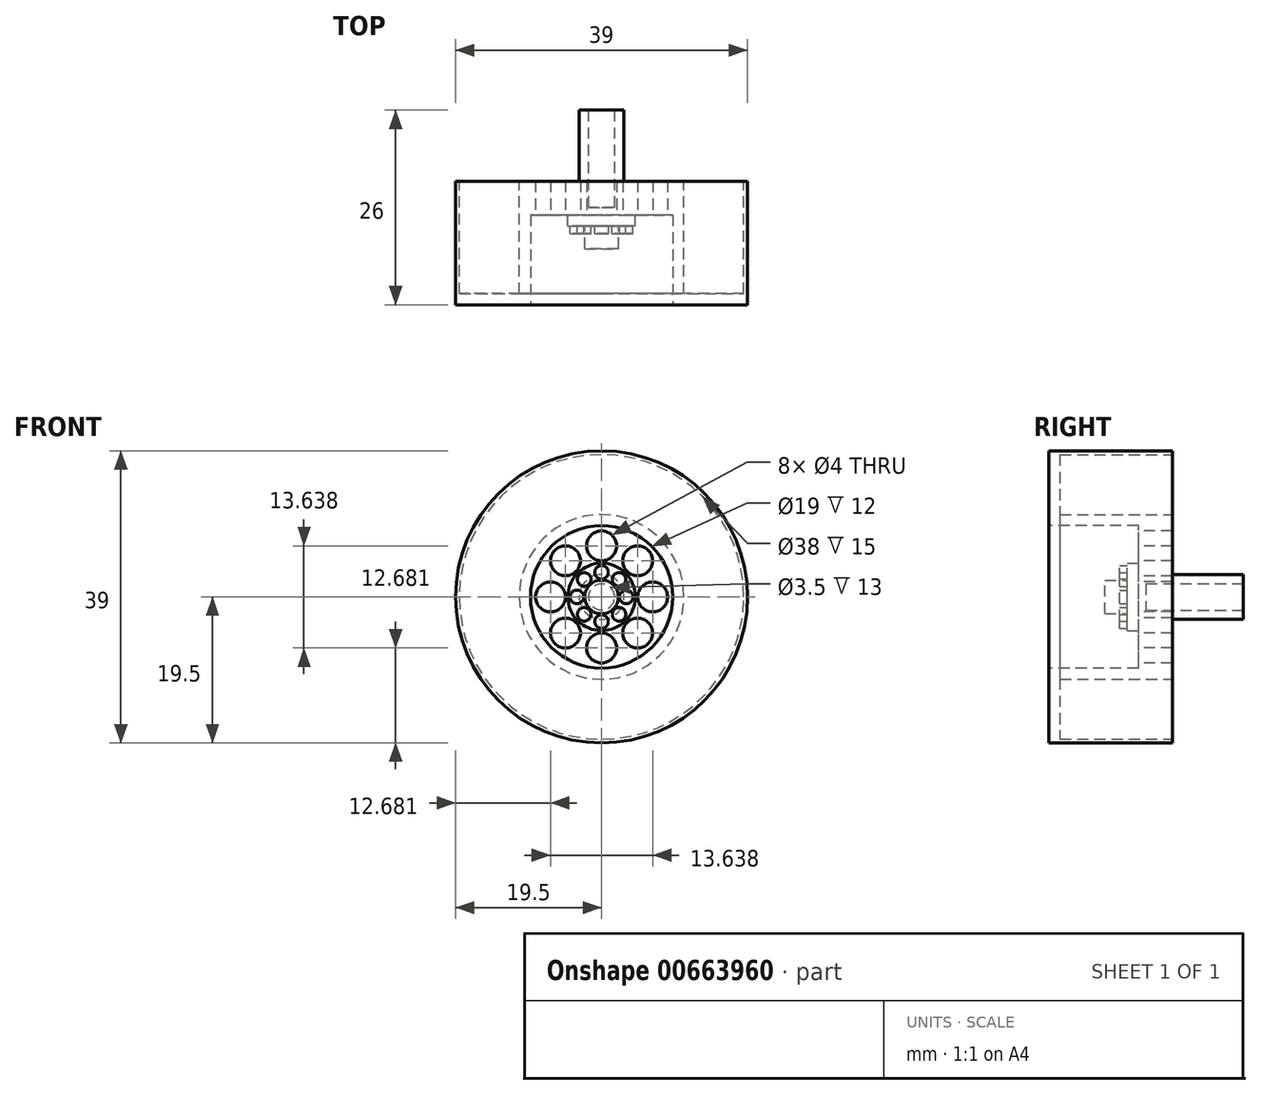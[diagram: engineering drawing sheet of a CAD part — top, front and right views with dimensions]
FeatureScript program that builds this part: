
annotation { "Feature Type Name" : "Feature", "Feature Type Description" : "" }
export const myFeature = defineFeature(function(context is Context, id is Id, definition is map)
    precondition{}
    {
        {
            var Q0;
            Q0=qCreatedBy(makeId("Front.planeOp"),FACE);
            var sketch = newSketch(context, id + "F0", { "sketchPlane" : qUnion([Q0])});
            skCircle(sketch, "E0", {"center": v(0, 0) * mm, "radius": 19.5 * mm});
            skSolve(sketch);
        }
        {
            var Q0;
            Q0=makeQuery(id+"F0.imprint","IMPRINT",FACE,{"disambiguationData":[TD([[makeQuery(id+"F0.imprint","IMPRINT",EDGE,{"derivedFrom":sQuery(id+"F0.wireOp",EDGE,"E0")}),1.0]])]});
            extrude(context, id + "F1", {"entities" : qUnion([Q0]), "oppositeDirection" : true, "depth" : 16.5 * mm, "offsetDistance" : 25 * mm});
        }
        {
            var Q0;
            Q0=qCreatedBy(makeId("Front.planeOp"),FACE);
            var sketch = newSketch(context, id + "F2", { "sketchPlane" : qUnion([Q0])});
            skCircle(sketch, "E1", {"center": v(0, 0) * mm, "radius": 9.5 * mm});
            skSolve(sketch);
        }
        {
            var Q0;
            Q0=makeQuery(id+"F2.imprint","IMPRINT",FACE,{"disambiguationData":[TD([[makeQuery(id+"F2.imprint","IMPRINT",EDGE,{"derivedFrom":sQuery(id+"F2.wireOp",EDGE,"E1")}),1.0]])]});
            var sketch = newSketch(context, id + "F3", { "sketchPlane" : qUnion([Q0])});
            skSolve(sketch);
        }
        {
            var Q0;
            Q0=makeQuery(id+"F3.imprint","IMPRINT",FACE,{"disambiguationData":[TD([[makeQuery(id+"F3.imprint","IMPRINT",EDGE,{"derivedFrom":makeQuery(id+"F2.imprint","IMPRINT",EDGE,{"derivedFrom":sQuery(id+"F2.wireOp",EDGE,"E1")})}),1.0]])]});
            extrude(context, id + "F4", {"entities" : qUnion([Q0]), "operationType" : NewBodyOperationType.REMOVE, "oppositeDirection" : true, "depth" : 12 * mm, "offsetDistance" : 25 * mm});
        }
        {
            var Q0;
            Q0=makeQuery(id+"F4.boolean.opBoolean","COPY",FACE,{"derivedFrom":makeQuery(id+"F4.opExtrude","CAP_FACE",FACE,{"disambiguationData":[OSD([sQuery(id+"F2.wireOp",EDGE,"E1")])],"isStart":false})});
            var sketch = newSketch(context, id + "F5", { "sketchPlane" : qUnion([Q0])});
            skCircle(sketch, "E2", {"center": v(0, 6.82) * mm, "radius": 2 * mm});
            skCircle(sketch, "E3.1.0", {"center": v(-4.82, 4.82) * mm, "radius": 2 * mm});
            skCircle(sketch, "E3.2.0", {"center": v(-6.82, 0) * mm, "radius": 2 * mm});
            skCircle(sketch, "E3.3.0", {"center": v(-4.82, -4.82) * mm, "radius": 2 * mm});
            skCircle(sketch, "E3.4.0", {"center": v(0, -6.82) * mm, "radius": 2 * mm});
            skCircle(sketch, "E3.5.0", {"center": v(4.82, -4.82) * mm, "radius": 2 * mm});
            skCircle(sketch, "E3.6.0", {"center": v(6.82, 0) * mm, "radius": 2 * mm});
            skCircle(sketch, "E3.7.0", {"center": v(4.82, 4.82) * mm, "radius": 2 * mm});
            skPoint(sketch, "E3.center", {"position": v(0, 0) * mm});
            skSolve(sketch);
        }
        {
            var Q0;
            Q0=makeQuery(id+"F5.imprint","IMPRINT",FACE,{"disambiguationData":[TD([[makeQuery(id+"F5.imprint","IMPRINT",EDGE,{"derivedFrom":sQuery(id+"F5.wireOp",EDGE,"E2")}),1.0]])]});
            var Q1;
            Q1=makeQuery(id+"F5.imprint","IMPRINT",FACE,{"disambiguationData":[TD([[makeQuery(id+"F5.imprint","IMPRINT",EDGE,{"derivedFrom":sQuery(id+"F5.wireOp",EDGE,"E3.7.0")}),1.0]])]});
            var Q2;
            Q2=makeQuery(id+"F5.imprint","IMPRINT",FACE,{"disambiguationData":[TD([[makeQuery(id+"F5.imprint","IMPRINT",EDGE,{"derivedFrom":sQuery(id+"F5.wireOp",EDGE,"E3.6.0")}),1.0]])]});
            var Q3;
            Q3=makeQuery(id+"F5.imprint","IMPRINT",FACE,{"disambiguationData":[TD([[makeQuery(id+"F5.imprint","IMPRINT",EDGE,{"derivedFrom":sQuery(id+"F5.wireOp",EDGE,"E3.5.0")}),1.0]])]});
            var Q4;
            Q4=makeQuery(id+"F5.imprint","IMPRINT",FACE,{"disambiguationData":[TD([[makeQuery(id+"F5.imprint","IMPRINT",EDGE,{"derivedFrom":sQuery(id+"F5.wireOp",EDGE,"E3.4.0")}),1.0]])]});
            var Q5;
            Q5=makeQuery(id+"F5.imprint","IMPRINT",FACE,{"disambiguationData":[TD([[makeQuery(id+"F5.imprint","IMPRINT",EDGE,{"derivedFrom":sQuery(id+"F5.wireOp",EDGE,"E3.3.0")}),1.0]])]});
            var Q6;
            Q6=makeQuery(id+"F5.imprint","IMPRINT",FACE,{"disambiguationData":[TD([[makeQuery(id+"F5.imprint","IMPRINT",EDGE,{"derivedFrom":sQuery(id+"F5.wireOp",EDGE,"E3.2.0")}),1.0]])]});
            var Q7;
            Q7=makeQuery(id+"F5.imprint","IMPRINT",FACE,{"disambiguationData":[TD([[makeQuery(id+"F5.imprint","IMPRINT",EDGE,{"derivedFrom":sQuery(id+"F5.wireOp",EDGE,"E3.1.0")}),1.0]])]});
            extrude(context, id + "F6", {"entities" : qUnion([Q0, Q1, Q2, Q3, Q4, Q5, Q6, Q7]), "operationType" : NewBodyOperationType.REMOVE, "oppositeDirection" : true, "depth" : 25 * mm, "offsetDistance" : 25 * mm});
        }
        {
            var Q0;
            Q0=makeQuery(id+"F4.boolean.opBoolean","COPY",FACE,{"derivedFrom":makeQuery(id+"F4.opExtrude","CAP_FACE",FACE,{"disambiguationData":[OSD([sQuery(id+"F2.wireOp",EDGE,"E1")])],"isStart":false})});
            var sketch = newSketch(context, id + "F7", { "sketchPlane" : qUnion([Q0])});
            skCircle(sketch, "E4", {"center": v(0, 0) * mm, "radius": 4.5 * mm});
            skSolve(sketch);
        }
        {
            var Q0;
            Q0=makeQuery(id+"F7.imprint","IMPRINT",FACE,{"disambiguationData":[TD([[makeQuery(id+"F7.imprint","IMPRINT",EDGE,{"derivedFrom":sQuery(id+"F7.wireOp",EDGE,"E4")}),1.0]])]});
            extrude(context, id + "F8", {"entities" : qUnion([Q0]), "operationType" : NewBodyOperationType.ADD, "depth" : 1.5 * mm, "offsetDistance" : 25 * mm});
        }
        {
            var Q0;
            Q0=makeQuery(id+"F8.opExtrude","CAP_FACE",FACE,{"disambiguationData":[OSD([sQuery(id+"F7.wireOp",EDGE,"E4")])],"isStart":false});
            var sketch = newSketch(context, id + "F9", { "sketchPlane" : qUnion([Q0])});
            skCircle(sketch, "E5", {"center": v(0, 0) * mm, "radius": 2.25 * mm});
            skSolve(sketch);
        }
        {
            var Q0;
            Q0=makeQuery(id+"F9.imprint","IMPRINT",FACE,{"disambiguationData":[TD([[makeQuery(id+"F9.imprint","IMPRINT",EDGE,{"derivedFrom":sQuery(id+"F9.wireOp",EDGE,"E5")}),1.0]])]});
            extrude(context, id + "F10", {"entities" : qUnion([Q0]), "operationType" : NewBodyOperationType.ADD, "depth" : 3 * mm, "offsetDistance" : 25 * mm});
        }
        {
            var Q0;
            Q0=makeQuery(id+"F8.opExtrude","CAP_FACE",FACE,{"disambiguationData":[OSD([sQuery(id+"F7.wireOp",EDGE,"E4")])],"isStart":false});
            var sketch = newSketch(context, id + "F11", { "sketchPlane" : qUnion([Q0])});
            skCircle(sketch, "E6", {"center": v(0, 3.29) * mm, "radius": 0.9 * mm});
            skCircle(sketch, "E7.1.0", {"center": v(-2.33, 2.33) * mm, "radius": 0.9 * mm});
            skCircle(sketch, "E7.2.0", {"center": v(-3.29, 0) * mm, "radius": 0.9 * mm});
            skCircle(sketch, "E7.3.0", {"center": v(-2.33, -2.33) * mm, "radius": 0.9 * mm});
            skCircle(sketch, "E7.4.0", {"center": v(0, -3.29) * mm, "radius": 0.9 * mm});
            skCircle(sketch, "E7.5.0", {"center": v(2.33, -2.33) * mm, "radius": 0.9 * mm});
            skCircle(sketch, "E7.6.0", {"center": v(3.29, 0) * mm, "radius": 0.9 * mm});
            skCircle(sketch, "E7.7.0", {"center": v(2.33, 2.33) * mm, "radius": 0.9 * mm});
            skPoint(sketch, "E7.center", {"position": v(0, 0) * mm});
            skSolve(sketch);
        }
        {
            var Q0;
            Q0=makeQuery(id+"F11.imprint","IMPRINT",FACE,{"disambiguationData":[TD([[makeQuery(id+"F11.imprint","IMPRINT",EDGE,{"derivedFrom":sQuery(id+"F11.wireOp",EDGE,"E6")}),1.0]])]});
            var Q1;
            Q1=makeQuery(id+"F11.imprint","IMPRINT",FACE,{"disambiguationData":[TD([[makeQuery(id+"F11.imprint","IMPRINT",EDGE,{"derivedFrom":sQuery(id+"F11.wireOp",EDGE,"E7.7.0")}),1.0]])]});
            var Q2;
            Q2=makeQuery(id+"F11.imprint","IMPRINT",FACE,{"disambiguationData":[TD([[makeQuery(id+"F11.imprint","IMPRINT",EDGE,{"derivedFrom":sQuery(id+"F11.wireOp",EDGE,"E7.6.0")}),1.0]])]});
            var Q3;
            Q3=makeQuery(id+"F11.imprint","IMPRINT",FACE,{"disambiguationData":[TD([[makeQuery(id+"F11.imprint","IMPRINT",EDGE,{"derivedFrom":sQuery(id+"F11.wireOp",EDGE,"E7.5.0")}),1.0]])]});
            var Q4;
            Q4=makeQuery(id+"F11.imprint","IMPRINT",FACE,{"disambiguationData":[TD([[makeQuery(id+"F11.imprint","IMPRINT",EDGE,{"derivedFrom":sQuery(id+"F11.wireOp",EDGE,"E7.4.0")}),1.0]])]});
            var Q5;
            Q5=makeQuery(id+"F11.imprint","IMPRINT",FACE,{"disambiguationData":[TD([[makeQuery(id+"F11.imprint","IMPRINT",EDGE,{"derivedFrom":sQuery(id+"F11.wireOp",EDGE,"E7.3.0")}),1.0]])]});
            var Q6;
            Q6=makeQuery(id+"F11.imprint","IMPRINT",FACE,{"disambiguationData":[TD([[makeQuery(id+"F11.imprint","IMPRINT",EDGE,{"derivedFrom":sQuery(id+"F11.wireOp",EDGE,"E7.2.0")}),1.0]])]});
            var Q7;
            Q7=makeQuery(id+"F11.imprint","IMPRINT",FACE,{"disambiguationData":[TD([[makeQuery(id+"F11.imprint","IMPRINT",EDGE,{"derivedFrom":sQuery(id+"F11.wireOp",EDGE,"E7.1.0")}),1.0]])]});
            extrude(context, id + "F12", {"entities" : qUnion([Q0, Q1, Q2, Q3, Q4, Q5, Q6, Q7]), "operationType" : NewBodyOperationType.ADD, "depth" : 1 * mm, "offsetDistance" : 25 * mm});
        }
        {
            var Q0;
            Q0=makeQuery(id+"F1.opExtrude","CAP_FACE",FACE,{"disambiguationData":[OSD([sQuery(id+"F0.wireOp",EDGE,"E0")])],"isStart":false});
            var sketch = newSketch(context, id + "F13", { "sketchPlane" : qUnion([Q0])});
            skCircle(sketch, "E8", {"center": v(0, 0) * mm, "radius": 11 * mm});
            skCircle(sketch, "E9", {"center": v(0, 0) * mm, "radius": 19 * mm});
            skSolve(sketch);
        }
        {
            var Q0;
            Q0=makeQuery(id+"F13.imprint","IMPRINT",FACE,{"disambiguationData":[TD([[makeQuery(id+"F13.imprint","IMPRINT",EDGE,{"derivedFrom":sQuery(id+"F13.wireOp",EDGE,"E8")}),-1.0]])]});
            extrude(context, id + "F14", {"entities" : qUnion([Q0]), "operationType" : NewBodyOperationType.REMOVE, "oppositeDirection" : true, "depth" : 15 * mm, "offsetDistance" : 25 * mm});
        }
        {
            var Q0;
            Q0=makeQuery(id+"F14.boolean.opBoolean","SPLIT",FACE,{"disambiguationData":[TD([makeQuery(id+"F6.boolean.opBoolean","COPY",FACE,{"derivedFrom":makeQuery(id+"F6.opExtrude","SWEPT_FACE",FACE,{"disambiguationData":[OSD([sQuery(id+"F5.wireOp",EDGE,"E2")])]})})])],"derivedFrom":makeQuery(id+"F1.opExtrude","CAP_FACE",FACE,{"disambiguationData":[OSD([sQuery(id+"F0.wireOp",EDGE,"E0")])],"isStart":false})});
            var sketch = newSketch(context, id + "F15", { "sketchPlane" : qUnion([Q0])});
            skCircle(sketch, "E10", {"center": v(0, 0) * mm, "radius": 3 * mm});
            skSolve(sketch);
        }
        {
            var Q0;
            Q0=makeQuery(id+"F15.imprint","IMPRINT",FACE,{"disambiguationData":[TD([[makeQuery(id+"F15.imprint","IMPRINT",EDGE,{"derivedFrom":sQuery(id+"F15.wireOp",EDGE,"E10")}),1.0]])]});
            extrude(context, id + "F16", {"entities" : qUnion([Q0]), "operationType" : NewBodyOperationType.ADD, "depth" : 9.5 * mm, "offsetDistance" : 25 * mm});
        }
        {
            var Q0;
            Q0=makeQuery(id+"F16.opExtrude","CAP_FACE",FACE,{"disambiguationData":[OSD([sQuery(id+"F15.wireOp",EDGE,"E10")])],"isStart":false});
            var sketch = newSketch(context, id + "F17", { "sketchPlane" : qUnion([Q0])});
            skCircle(sketch, "E11", {"center": v(0, 0) * mm, "radius": 1.75 * mm});
            skSolve(sketch);
        }
        {
            var Q0;
            Q0=makeQuery(id+"F17.imprint","IMPRINT",FACE,{"disambiguationData":[TD([[makeQuery(id+"F17.imprint","IMPRINT",EDGE,{"derivedFrom":sQuery(id+"F17.wireOp",EDGE,"E11")}),1.0]])]});
            extrude(context, id + "F18", {"entities" : qUnion([Q0]), "operationType" : NewBodyOperationType.REMOVE, "oppositeDirection" : true, "depth" : 13 * mm, "offsetDistance" : 25 * mm});
        }
    });
